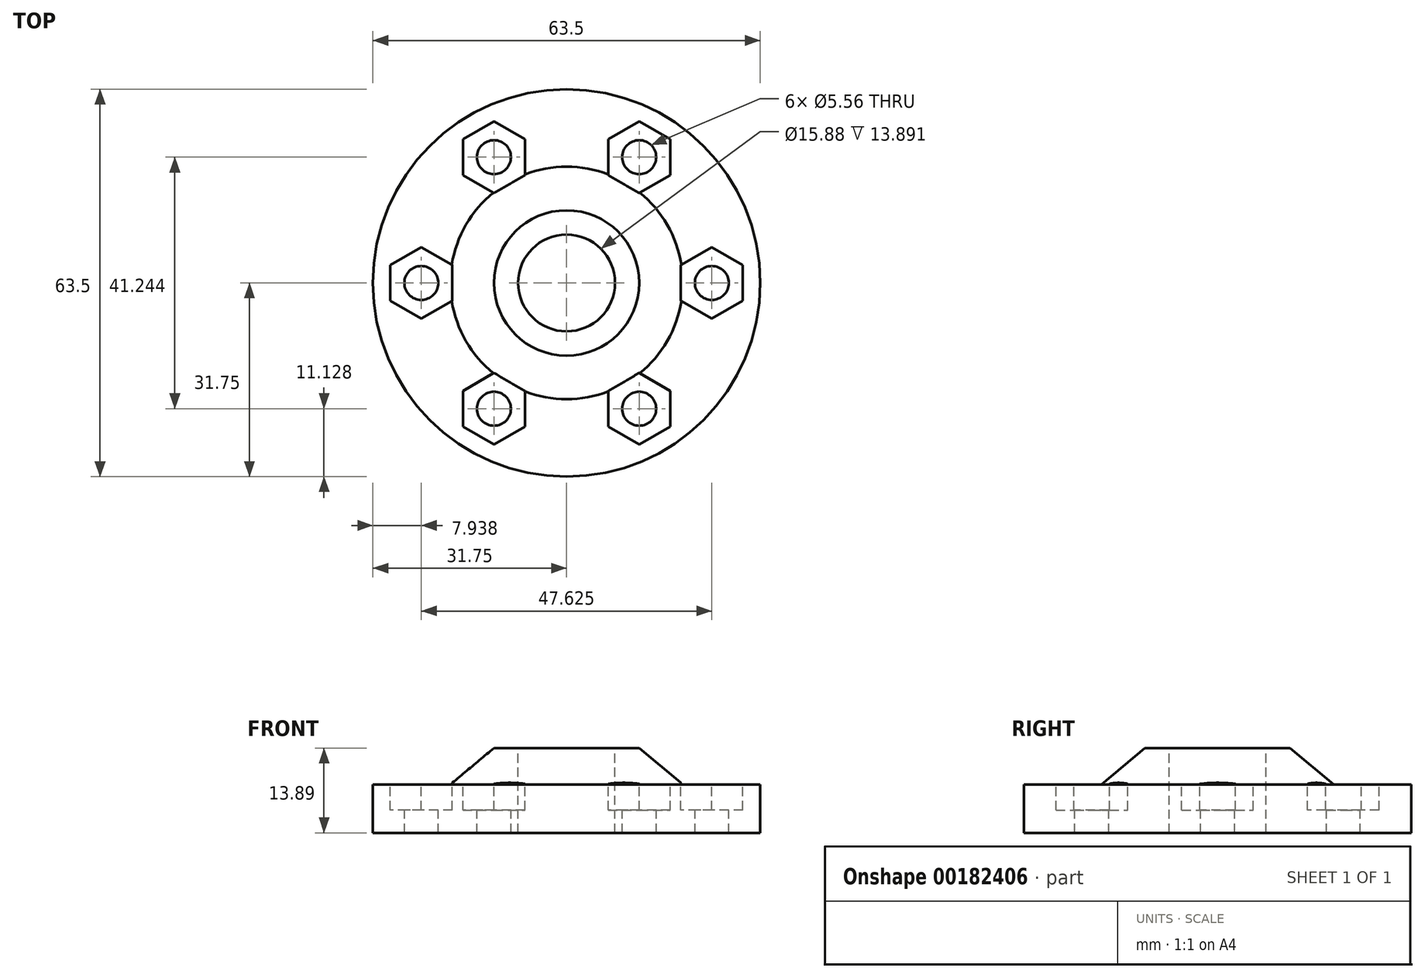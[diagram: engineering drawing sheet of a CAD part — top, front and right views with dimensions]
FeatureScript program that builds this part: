
annotation { "Feature Type Name" : "Feature", "Feature Type Description" : "" }
export const myFeature = defineFeature(function(context is Context, id is Id, definition is map)
    precondition{}
    {
        {
            var Q0;
            Q0=qCreatedBy(makeId("Front.planeOp"),FACE);
            var sketch = newSketch(context, id + "F0", { "sketchPlane" : qUnion([Q0])});
            skLineSegment(sketch, "E0", {"start": v(0, 0) * mm, "end": v(-31.75, 0) * mm});
            skLineSegment(sketch, "E1", {"start": v(-31.75, 0) * mm, "end": v(-31.75, 7.94) * mm});
            skLineSegment(sketch, "E2", {"start": v(-31.75, 7.94) * mm, "end": v(-19.05, 7.94) * mm});
            skLineSegment(sketch, "E3", {"start": v(0, 0) * mm, "end": v(0, 13.9) * mm});
            skLineSegment(sketch, "E4", {"start": v(0, 13.9) * mm, "end": v(-11.9, 13.9) * mm});
            skLineSegment(sketch, "E5", {"start": v(-11.9, 13.9) * mm, "end": v(-19.05, 7.94) * mm});
            skSolve(sketch);
        }
        {
            var Q0;
            Q0=makeQuery(id+"F0.imprint","IMPRINT",FACE,{"disambiguationData":[TD([[makeQuery(id+"F0.imprint","IMPRINT",EDGE,{"derivedFrom":sQuery(id+"F0.wireOp",EDGE,"E0")}),-1.0]])]});
            var Q1;
            Q1=sQuery(id+"F0.wireOp",EDGE,"E3");
            revolve(context, id + "F1", {"entities" : qUnion([Q0]), "axis" : qUnion([Q1]), "revolveType" : RevolveType.FULL});
        }
        {
            var Q0;
            Q0=makeQuery(id+"F1.opRevolve","SWEPT_FACE",FACE,{"disambiguationData":[OSD([sQuery(id+"F0.wireOp",EDGE,"E4")])]});
            var sketch = newSketch(context, id + "F2", { "sketchPlane" : qUnion([Q0])});
            skCircle(sketch, "E6", {"center": v(0, 0) * mm, "radius": 7.94 * mm});
            skLineSegment(sketch, "E7", {"start": v(0, 0) * mm, "end": v(23.81, 0) * mm});
            skCircle(sketch, "E8", {"center": v(23.81, 0) * mm, "radius": 2.78 * mm});
            skCircle(sketch, "E9.cCircle", {"center": v(23.81, 0) * mm, "radius": 5.08 * mm, "construction": true});
            skLineSegment(sketch, "E9.0", {"start": v(18.73, -2.93) * mm, "end": v(18.73, 2.93) * mm});
            skLineSegment(sketch, "E9.1", {"start": v(18.73, 2.93) * mm, "end": v(23.81, 5.87) * mm});
            skLineSegment(sketch, "E9.2", {"start": v(23.81, 5.87) * mm, "end": v(28.9, 2.93) * mm});
            skLineSegment(sketch, "E9.3", {"start": v(28.9, 2.93) * mm, "end": v(28.9, -2.93) * mm});
            skLineSegment(sketch, "E9.4", {"start": v(28.9, -2.93) * mm, "end": v(23.81, -5.87) * mm});
            skLineSegment(sketch, "E9.5", {"start": v(23.81, -5.87) * mm, "end": v(18.73, -2.93) * mm});
            skPoint(sketch, "E9.0.midPoint", {"position": v(18.73, 0) * mm});
            skLineSegment(sketch, "E10.1.0", {"start": v(6.83, 23.56) * mm, "end": v(11.9, 26.49) * mm});
            skLineSegment(sketch, "E10.1.1", {"start": v(11.9, 26.49) * mm, "end": v(16.99, 23.56) * mm});
            skLineSegment(sketch, "E10.1.2", {"start": v(16.99, 23.56) * mm, "end": v(16.99, 17.69) * mm});
            skLineSegment(sketch, "E10.1.3", {"start": v(16.99, 17.69) * mm, "end": v(11.9, 14.76) * mm});
            skLineSegment(sketch, "E10.1.4", {"start": v(11.9, 14.76) * mm, "end": v(6.83, 17.69) * mm});
            skLineSegment(sketch, "E10.1.5", {"start": v(6.83, 17.69) * mm, "end": v(6.83, 23.56) * mm});
            skCircle(sketch, "E10.1.6", {"center": v(11.9, 20.62) * mm, "radius": 2.78 * mm});
            skLineSegment(sketch, "E10.2.0", {"start": v(-16.99, 17.69) * mm, "end": v(-16.99, 23.56) * mm});
            skLineSegment(sketch, "E10.2.1", {"start": v(-16.99, 23.56) * mm, "end": v(-11.9, 26.49) * mm});
            skLineSegment(sketch, "E10.2.2", {"start": v(-11.9, 26.49) * mm, "end": v(-6.83, 23.56) * mm});
            skLineSegment(sketch, "E10.2.3", {"start": v(-6.83, 23.56) * mm, "end": v(-6.83, 17.69) * mm});
            skLineSegment(sketch, "E10.2.4", {"start": v(-6.83, 17.69) * mm, "end": v(-11.9, 14.76) * mm});
            skLineSegment(sketch, "E10.2.5", {"start": v(-11.9, 14.76) * mm, "end": v(-16.99, 17.69) * mm});
            skCircle(sketch, "E10.2.6", {"center": v(-11.9, 20.62) * mm, "radius": 2.78 * mm});
            skLineSegment(sketch, "E10.3.0", {"start": v(-23.81, -5.87) * mm, "end": v(-28.9, -2.93) * mm});
            skLineSegment(sketch, "E10.3.1", {"start": v(-28.9, -2.93) * mm, "end": v(-28.9, 2.93) * mm});
            skLineSegment(sketch, "E10.3.2", {"start": v(-28.9, 2.93) * mm, "end": v(-23.81, 5.87) * mm});
            skLineSegment(sketch, "E10.3.3", {"start": v(-23.81, 5.87) * mm, "end": v(-18.73, 2.93) * mm});
            skLineSegment(sketch, "E10.3.4", {"start": v(-18.73, 2.93) * mm, "end": v(-18.73, -2.93) * mm});
            skLineSegment(sketch, "E10.3.5", {"start": v(-18.73, -2.93) * mm, "end": v(-23.81, -5.87) * mm});
            skCircle(sketch, "E10.3.6", {"center": v(-23.81, 0) * mm, "radius": 2.78 * mm});
            skLineSegment(sketch, "E10.4.0", {"start": v(-6.83, -23.56) * mm, "end": v(-11.9, -26.49) * mm});
            skLineSegment(sketch, "E10.4.1", {"start": v(-11.9, -26.49) * mm, "end": v(-16.99, -23.56) * mm});
            skLineSegment(sketch, "E10.4.2", {"start": v(-16.99, -23.56) * mm, "end": v(-16.99, -17.69) * mm});
            skLineSegment(sketch, "E10.4.3", {"start": v(-16.99, -17.69) * mm, "end": v(-11.9, -14.76) * mm});
            skLineSegment(sketch, "E10.4.4", {"start": v(-11.9, -14.76) * mm, "end": v(-6.83, -17.69) * mm});
            skLineSegment(sketch, "E10.4.5", {"start": v(-6.83, -17.69) * mm, "end": v(-6.83, -23.56) * mm});
            skCircle(sketch, "E10.4.6", {"center": v(-11.9, -20.62) * mm, "radius": 2.78 * mm});
            skLineSegment(sketch, "E10.5.0", {"start": v(16.99, -17.69) * mm, "end": v(16.99, -23.56) * mm});
            skLineSegment(sketch, "E10.5.1", {"start": v(16.99, -23.56) * mm, "end": v(11.9, -26.49) * mm});
            skLineSegment(sketch, "E10.5.2", {"start": v(11.9, -26.49) * mm, "end": v(6.83, -23.56) * mm});
            skLineSegment(sketch, "E10.5.3", {"start": v(6.83, -23.56) * mm, "end": v(6.83, -17.69) * mm});
            skLineSegment(sketch, "E10.5.4", {"start": v(6.83, -17.69) * mm, "end": v(11.9, -14.76) * mm});
            skLineSegment(sketch, "E10.5.5", {"start": v(11.9, -14.76) * mm, "end": v(16.99, -17.69) * mm});
            skCircle(sketch, "E10.5.6", {"center": v(11.9, -20.62) * mm, "radius": 2.78 * mm});
            skSolve(sketch);
        }
        {
            var Q0;
            Q0=makeQuery(id+"F2.imprint","IMPRINT",FACE,{"disambiguationData":[TD([[makeQuery(id+"F2.imprint","IMPRINT",EDGE,{"derivedFrom":sQuery(id+"F2.wireOp",EDGE,"E6")}),1.0]])]});
            var Q1;
            Q1=makeQuery(id+"F2.imprint","IMPRINT",FACE,{"disambiguationData":[TD([[makeQuery(id+"F2.imprint","IMPRINT",EDGE,{"derivedFrom":sQuery(id+"F2.wireOp",EDGE,"E10.2.6")}),1.0]])]});
            var Q2;
            Q2=makeQuery(id+"F2.imprint","IMPRINT",FACE,{"disambiguationData":[TD([[makeQuery(id+"F2.imprint","IMPRINT",EDGE,{"derivedFrom":sQuery(id+"F2.wireOp",EDGE,"E10.1.6")}),1.0]])]});
            var Q3;
            Q3=makeQuery(id+"F2.imprint","IMPRINT",FACE,{"disambiguationData":[TD([[makeQuery(id+"F2.imprint","IMPRINT",EDGE,{"derivedFrom":sQuery(id+"F2.wireOp",EDGE,"E8")}),1.0]])]});
            var Q4;
            Q4=makeQuery(id+"F2.imprint","IMPRINT",FACE,{"disambiguationData":[TD([[makeQuery(id+"F2.imprint","IMPRINT",EDGE,{"derivedFrom":sQuery(id+"F2.wireOp",EDGE,"E10.5.6")}),1.0]])]});
            var Q5;
            Q5=makeQuery(id+"F2.imprint","IMPRINT",FACE,{"disambiguationData":[TD([[makeQuery(id+"F2.imprint","IMPRINT",EDGE,{"derivedFrom":sQuery(id+"F2.wireOp",EDGE,"E10.4.6")}),1.0]])]});
            var Q6;
            Q6=makeQuery(id+"F2.imprint","IMPRINT",FACE,{"disambiguationData":[TD([[makeQuery(id+"F2.imprint","IMPRINT",EDGE,{"derivedFrom":sQuery(id+"F2.wireOp",EDGE,"E10.3.6")}),1.0]])]});
            extrude(context, id + "F3", {"entities" : qUnion([Q0, Q1, Q2, Q3, Q4, Q5, Q6]), "operationType" : NewBodyOperationType.REMOVE, "oppositeDirection" : true, "depth" : 25.4 * mm});
        }
        {
            var Q0;
            Q0=makeQuery(id+"F2.imprint","IMPRINT",FACE,{"disambiguationData":[TD([[makeQuery(id+"F2.imprint","IMPRINT",EDGE,{"derivedFrom":sQuery(id+"F2.wireOp",EDGE,"E10.2.0")}),-1.0]])]});
            var Q1;
            Q1=makeQuery(id+"F2.imprint","IMPRINT",FACE,{"disambiguationData":[TD([[makeQuery(id+"F2.imprint","IMPRINT",EDGE,{"derivedFrom":sQuery(id+"F2.wireOp",EDGE,"E10.1.0")}),-1.0]])]});
            var Q2;
            Q2=makeQuery(id+"F2.imprint","IMPRINT",FACE,{"disambiguationData":[TD([[makeQuery(id+"F2.imprint","IMPRINT",EDGE,{"derivedFrom":sQuery(id+"F2.wireOp",EDGE,"E8")}),-1.0]])]});
            var Q3;
            Q3=makeQuery(id+"F2.imprint","IMPRINT",FACE,{"disambiguationData":[TD([[makeQuery(id+"F2.imprint","IMPRINT",EDGE,{"derivedFrom":sQuery(id+"F2.wireOp",EDGE,"E10.5.0")}),-1.0]])]});
            var Q4;
            Q4=makeQuery(id+"F2.imprint","IMPRINT",FACE,{"disambiguationData":[TD([[makeQuery(id+"F2.imprint","IMPRINT",EDGE,{"derivedFrom":sQuery(id+"F2.wireOp",EDGE,"E10.4.0")}),-1.0]])]});
            var Q5;
            Q5=makeQuery(id+"F2.imprint","IMPRINT",FACE,{"disambiguationData":[TD([[makeQuery(id+"F2.imprint","IMPRINT",EDGE,{"derivedFrom":sQuery(id+"F2.wireOp",EDGE,"E10.3.0")}),-1.0]])]});
            extrude(context, id + "F4", {"entities" : qUnion([Q0, Q1, Q2, Q3, Q4, Q5]), "operationType" : NewBodyOperationType.REMOVE, "oppositeDirection" : true, "depth" : 10.16 * mm});
        }
    });
